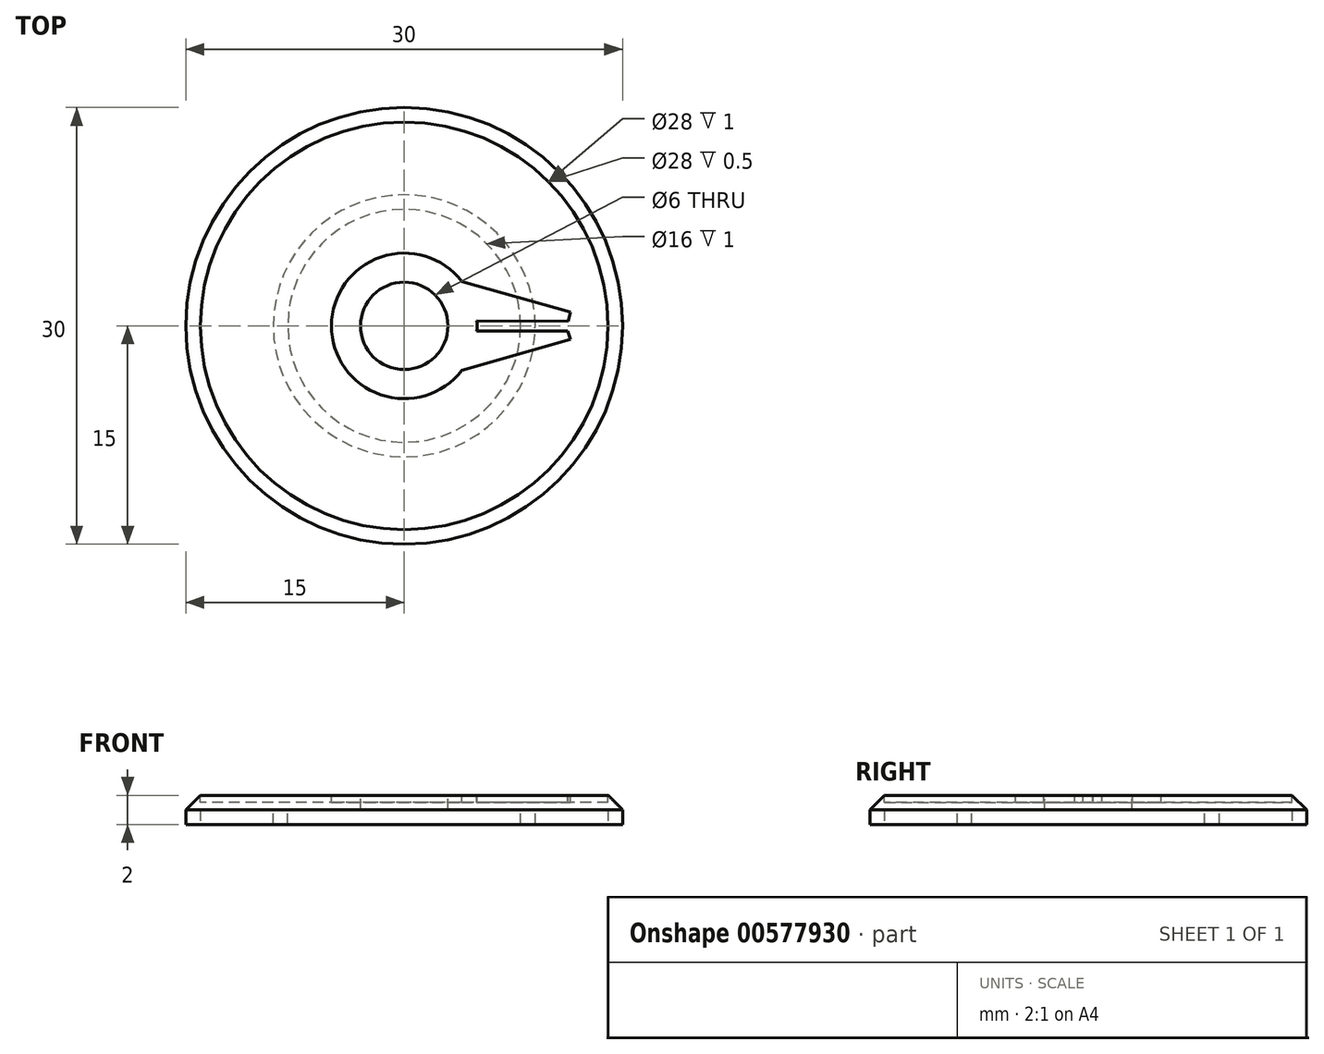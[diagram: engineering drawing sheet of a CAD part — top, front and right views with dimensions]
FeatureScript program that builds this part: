
annotation { "Feature Type Name" : "Feature", "Feature Type Description" : "" }
export const myFeature = defineFeature(function(context is Context, id is Id, definition is map)
    precondition{}
    {
        {
            var Q0;
            Q0=qCreatedBy(makeId("Top.planeOp"),FACE);
            var sketch = newSketch(context, id + "F0", { "sketchPlane" : qUnion([Q0])});
            skCircle(sketch, "E0", {"center": v(0, 0) * mm, "radius": 15 * mm});
            skSolve(sketch);
        }
        {
            var Q0;
            Q0=makeQuery(id+"F0.imprint","IMPRINT",FACE,{"disambiguationData":[TD([[makeQuery(id+"F0.imprint","IMPRINT",EDGE,{"derivedFrom":sQuery(id+"F0.wireOp",EDGE,"E0")}),1.0]])]});
            var Q1;
            Q1=sQuery(id+"F0.wireOp",EDGE,"E0");
            extrude(context, id + "F1", {"entities" : qUnion([Q0]), "surfaceEntities" : qUnion([Q1]), "depth" : 2 * mm, "offsetDistance" : 25 * mm});
        }
        {
            var Q0;
            Q0=makeQuery(id+"F1.opExtrude","CAP_FACE",FACE,{"disambiguationData":[OSD([sQuery(id+"F0.wireOp",EDGE,"E0")])],"isStart":true});
            var sketch = newSketch(context, id + "F2", { "sketchPlane" : qUnion([Q0])});
            skCircle(sketch, "E1", {"center": v(0, 0) * mm, "radius": 14 * mm});
            skSolve(sketch);
        }
        {
            var Q0;
            Q0=makeQuery(id+"F2.imprint","IMPRINT",FACE,{"disambiguationData":[TD([[makeQuery(id+"F2.imprint","IMPRINT",EDGE,{"derivedFrom":sQuery(id+"F2.wireOp",EDGE,"E1")}),1.0]])]});
            extrude(context, id + "F3", {"entities" : qUnion([Q0]), "operationType" : NewBodyOperationType.REMOVE, "oppositeDirection" : true, "depth" : 1 * mm, "offsetDistance" : 25 * mm});
        }
        {
            var Q0;
            Q0=makeQuery(id+"F1.opExtrude","CAP_EDGE",EDGE,{"disambiguationData":[OSD([sQuery(id+"F0.wireOp",EDGE,"E0")])],"isStart":false});
            chamfer(context, id + "F4", {"entities" : qUnion([Q0]), "width" : 1 * mm, "tangentPropagation" : true});
        }
        {
            var Q0;
            Q0=makeQuery(id+"F1.opExtrude","CAP_FACE",FACE,{"disambiguationData":[OSD([sQuery(id+"F0.wireOp",EDGE,"E0")])],"isStart":false});
            var sketch = newSketch(context, id + "F5", { "sketchPlane" : qUnion([Q0])});
            skCircle(sketch, "E2", {"center": v(0, 0) * mm, "radius": 4 * mm});
            skSolve(sketch);
        }
        {
            var Q0;
            Q0=makeQuery(id+"F5.imprint","IMPRINT",FACE,{"disambiguationData":[TD([[makeQuery(id+"F5.imprint","IMPRINT",EDGE,{"derivedFrom":sQuery(id+"F5.wireOp",EDGE,"E2")}),1.0]])]});
            extrude(context, id + "F6", {"entities" : qUnion([Q0]), "operationType" : NewBodyOperationType.REMOVE, "oppositeDirection" : true, "depth" : 25 * mm, "offsetDistance" : 25 * mm});
        }
        {
            var Q0;
            Q0=makeQuery(id+"F1.opExtrude","CAP_FACE",FACE,{"disambiguationData":[OSD([sQuery(id+"F0.wireOp",EDGE,"E0")])],"isStart":false});
            var sketch = newSketch(context, id + "F7", { "sketchPlane" : qUnion([Q0])});
            skCircle(sketch, "E3", {"center": v(0, 0) * mm, "radius": 14 * mm});
            skSolve(sketch);
        }
        {
            var Q0;
            Q0=makeQuery(id+"F7.imprint","IMPRINT",FACE,{"disambiguationData":[TD([[makeQuery(id+"F7.imprint","IMPRINT",EDGE,{"derivedFrom":sQuery(id+"F7.wireOp",EDGE,"E3")}),1.0]])]});
            var sketch = newSketch(context, id + "F8", { "sketchPlane" : qUnion([Q0])});
            skCircle(sketch, "E4", {"center": v(0, 0) * mm, "radius": 5 * mm});
            skLineSegment(sketch, "E5", {"start": v(3.96, -3.06) * mm, "end": v(11.41, -0.93) * mm});
            skLineSegment(sketch, "E6", {"start": v(11.41, -0.93) * mm, "end": v(11.24, -0.35) * mm});
            skLineSegment(sketch, "E7", {"start": v(11.24, -0.35) * mm, "end": v(4.99, -0.35) * mm});
            skLineSegment(sketch, "E8", {"start": v(4.99, -0.35) * mm, "end": v(4.99, 0.35) * mm});
            skLineSegment(sketch, "E9", {"start": v(4.99, 0.35) * mm, "end": v(11.25, 0.3) * mm});
            skLineSegment(sketch, "E10", {"start": v(11.25, 0.3) * mm, "end": v(11.43, 0.96) * mm});
            skLineSegment(sketch, "E11", {"start": v(11.43, 0.96) * mm, "end": v(3.96, 3.05) * mm});
            skSolve(sketch);
        }
        {
            var Q0;
            {var subQ0=sQuery(id+"F8.wireOp",EDGE,"E5");Q0=makeQuery(id+"F8.imprint","IMPRINT",FACE,{"disambiguationData":[TD([[makeQuery(id+"F8.imprint","IMPRINT",EDGE,{"derivedFrom":subQ0}),-1.0]])]});}
            extrude(context, id + "F9", {"entities" : qUnion([Q0]), "operationType" : NewBodyOperationType.REMOVE, "oppositeDirection" : true, "depth" : 0.5 * mm, "offsetDistance" : 25 * mm});
        }
        {
            var Q0;
            Q0=makeQuery(id+"F7.imprint","IMPRINT",FACE,{"disambiguationData":[TD([[makeQuery(id+"F7.imprint","IMPRINT",EDGE,{"derivedFrom":sQuery(id+"F7.wireOp",EDGE,"E3")}),1.0]])]});
            var sketch = newSketch(context, id + "F10", { "sketchPlane" : qUnion([Q0])});
            skCircle(sketch, "E12", {"center": v(0, 0) * mm, "radius": 3 * mm});
            skSolve(sketch);
        }
        {
            var Q0;
            Q0=makeQuery(id+"F10.imprint","IMPRINT",FACE,{"disambiguationData":[TD([[makeQuery(id+"F10.imprint","IMPRINT",EDGE,{"derivedFrom":sQuery(id+"F10.wireOp",EDGE,"E12")}),-1.0]])]});
            extrude(context, id + "F11", {"entities" : qUnion([Q0]), "operationType" : NewBodyOperationType.ADD, "depth" : -1 * mm, "offsetDistance" : 25 * mm});
        }
        {
            var Q0;
            Q0=makeQuery(id+"F11.boolean.opBoolean","MERGE",FACE,{"derivedFrom":[makeQuery(id+"F3.boolean.opBoolean","COPY",FACE,{"derivedFrom":makeQuery(id+"F3.opExtrude","CAP_FACE",FACE,{"disambiguationData":[OSD([sQuery(id+"F2.wireOp",EDGE,"E1")])],"isStart":false})}),makeQuery(id+"F11.opExtrude","CAP_FACE",FACE,{"disambiguationData":[OSD([sQuery(id+"F5.wireOp",EDGE,"E2"),sQuery(id+"F10.wireOp",EDGE,"E12")])],"isStart":false})]});
            var sketch = newSketch(context, id + "F12", { "sketchPlane" : qUnion([Q0])});
            skCircle(sketch, "E13", {"center": v(0, 0) * mm, "radius": 8 * mm});
            skCircle(sketch, "E14", {"center": v(0, 0) * mm, "radius": 9 * mm});
            skSolve(sketch);
        }
        {
            var Q0;
            Q0=makeQuery(id+"F12.imprint","IMPRINT",FACE,{"disambiguationData":[TD([[makeQuery(id+"F12.imprint","IMPRINT",EDGE,{"derivedFrom":sQuery(id+"F12.wireOp",EDGE,"E13")}),-1.0]])]});
            extrude(context, id + "F13", {"entities" : qUnion([Q0]), "operationType" : NewBodyOperationType.ADD, "depth" : 1 * mm, "offsetDistance" : 25 * mm});
        }
    });
